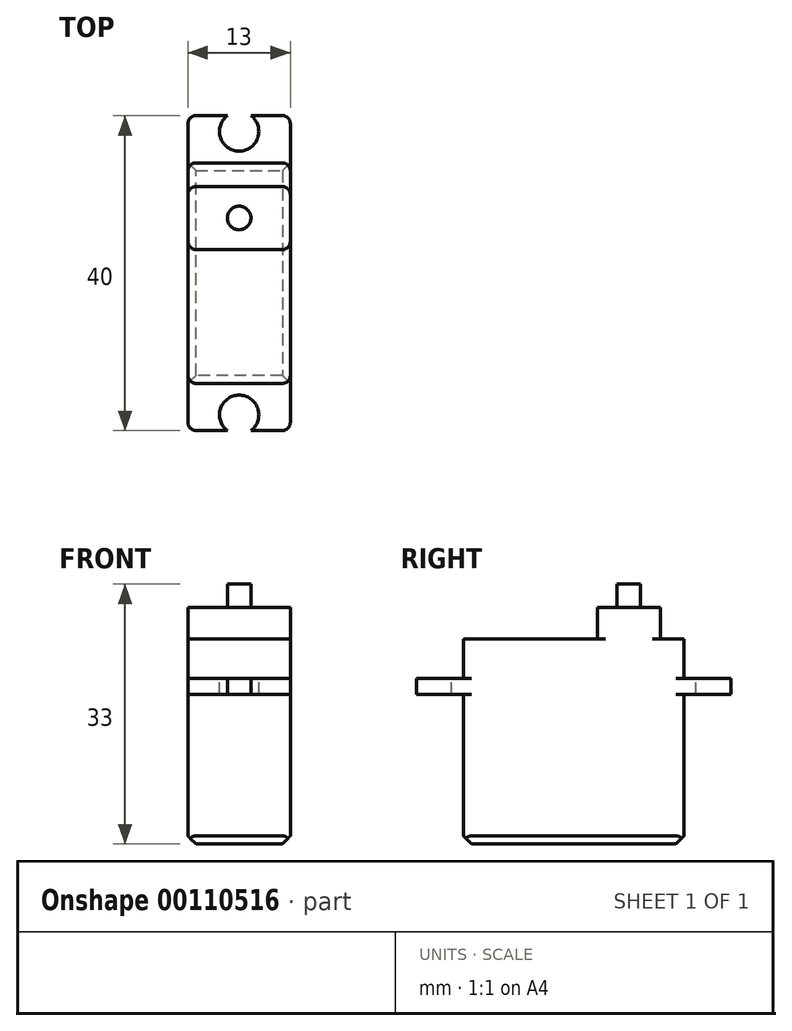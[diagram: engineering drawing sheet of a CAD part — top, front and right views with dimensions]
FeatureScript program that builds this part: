
annotation { "Feature Type Name" : "Feature", "Feature Type Description" : "" }
export const myFeature = defineFeature(function(context is Context, id is Id, definition is map)
    precondition{}
    {
        {
            var Q0;
            Q0=qCreatedBy(makeId("Right.planeOp"),FACE);
            var sketch = newSketch(context, id + "F0", { "sketchPlane" : qUnion([Q0])});
            skLineSegment(sketch, "E0", {"start": v(0, 19) * mm, "end": v(0, 0) * mm});
            skLineSegment(sketch, "E1", {"start": v(0, 0) * mm, "end": v(-28, 0) * mm});
            skLineSegment(sketch, "E2", {"start": v(-28, 0) * mm, "end": v(-28, 19) * mm});
            skLineSegment(sketch, "E3", {"start": v(-28, 19) * mm, "end": v(-34, 19) * mm});
            skLineSegment(sketch, "E4", {"start": v(-34, 19) * mm, "end": v(-34, 21) * mm});
            skLineSegment(sketch, "E5", {"start": v(6, 21) * mm, "end": v(6, 19) * mm});
            skLineSegment(sketch, "E6", {"start": v(6, 19) * mm, "end": v(0, 19) * mm});
            skLineSegment(sketch, "E7", {"start": v(-34, 21) * mm, "end": v(-28, 21) * mm});
            skLineSegment(sketch, "E8", {"start": v(-28, 21) * mm, "end": v(-28, 26) * mm});
            skLineSegment(sketch, "E9", {"start": v(-28, 26) * mm, "end": v(0, 26) * mm});
            skLineSegment(sketch, "E10", {"start": v(0, 26) * mm, "end": v(0, 21) * mm});
            skLineSegment(sketch, "E11", {"start": v(0, 21) * mm, "end": v(6, 21) * mm});
            skLineSegment(sketch, "E12", {"start": v(-11, 26) * mm, "end": v(-11, 30) * mm});
            skLineSegment(sketch, "E13", {"start": v(-11, 30) * mm, "end": v(-3, 30) * mm});
            skLineSegment(sketch, "E14", {"start": v(-3, 30) * mm, "end": v(-3, 26) * mm});
            skLineSegment(sketch, "E15", {"start": v(-7, 30) * mm, "end": v(-7, 0) * mm, "construction": true});
            skSolve(sketch);
        }
        {
            var Q0;
            Q0 = qSketchRegion(id + "F0", true);
            extrude(context, id + "F1", {"entities" : qUnion([Q0]), "endBound" : BoundingType.SYMMETRIC, "depth" : 13 * mm});
        }
        {
            var Q0;
            Q0=makeQuery(id+"F1.opExtrude","SWEPT_FACE",FACE,{"disambiguationData":[OSD([sQuery(id+"F0.wireOp",EDGE,"E13")])]});
            var sketch = newSketch(context, id + "F2", { "sketchPlane" : qUnion([Q0])});
            skCircle(sketch, "E16", {"center": v(0, -7) * mm, "radius": 1.5 * mm});
            skPoint(sketch, "E16.centerSnap0", {"position": v(6.5, -7) * mm});
            skSolve(sketch);
        }
        {
            var Q0;
            Q0 = qSketchRegion(id + "F2", true);
            extrude(context, id + "F3", {"entities" : qUnion([Q0]), "operationType" : NewBodyOperationType.ADD, "depth" : 3 * mm});
        }
        {
            var Q0;
            Q0=makeQuery(id+"F1.opExtrude","SWEPT_FACE",FACE,{"disambiguationData":[OSD([sQuery(id+"F0.wireOp",EDGE,"E1")])]});
            chamfer(context, id + "F4", {"entities" : qUnion([Q0]), "width" : 1 * mm, "tangentPropagation" : true});
        }
        {
            var Q0;
            Q0=makeQuery(id+"F1.opExtrude","CAP_EDGE",EDGE,{"disambiguationData":[OSD([sQuery(id+"F0.wireOp",EDGE,"E0")])],"isStart":false});
            var Q1;
            Q1=makeQuery(id+"F1.opExtrude","CAP_EDGE",EDGE,{"disambiguationData":[OSD([sQuery(id+"F0.wireOp",EDGE,"E10")])],"isStart":false});
            var Q2;
            Q2=makeQuery(id+"F1.opExtrude","CAP_EDGE",EDGE,{"disambiguationData":[OSD([sQuery(id+"F0.wireOp",EDGE,"E10")])],"isStart":true});
            var Q3;
            Q3=makeQuery(id+"F1.opExtrude","CAP_EDGE",EDGE,{"disambiguationData":[OSD([sQuery(id+"F0.wireOp",EDGE,"E14")])],"isStart":false});
            var Q4;
            Q4=makeQuery(id+"F1.opExtrude","CAP_EDGE",EDGE,{"disambiguationData":[OSD([sQuery(id+"F0.wireOp",EDGE,"E12")])],"isStart":false});
            var Q5;
            Q5=makeQuery(id+"F1.opExtrude","CAP_EDGE",EDGE,{"disambiguationData":[OSD([sQuery(id+"F0.wireOp",EDGE,"E12")])],"isStart":true});
            var Q6;
            Q6=makeQuery(id+"F1.opExtrude","CAP_EDGE",EDGE,{"disambiguationData":[OSD([sQuery(id+"F0.wireOp",EDGE,"E14")])],"isStart":true});
            var Q7;
            Q7=makeQuery(id+"F1.opExtrude","CAP_EDGE",EDGE,{"disambiguationData":[OSD([sQuery(id+"F0.wireOp",EDGE,"E8")])],"isStart":false});
            var Q8;
            Q8=makeQuery(id+"F1.opExtrude","CAP_EDGE",EDGE,{"disambiguationData":[OSD([sQuery(id+"F0.wireOp",EDGE,"E8")])],"isStart":true});
            var Q9;
            Q9=makeQuery(id+"F1.opExtrude","CAP_EDGE",EDGE,{"disambiguationData":[OSD([sQuery(id+"F0.wireOp",EDGE,"E4")])],"isStart":false});
            var Q10;
            Q10=makeQuery(id+"F1.opExtrude","CAP_EDGE",EDGE,{"disambiguationData":[OSD([sQuery(id+"F0.wireOp",EDGE,"E4")])],"isStart":true});
            var Q11;
            Q11=makeQuery(id+"F1.opExtrude","CAP_EDGE",EDGE,{"disambiguationData":[OSD([sQuery(id+"F0.wireOp",EDGE,"E2")])],"isStart":false});
            var Q12;
            Q12=makeQuery(id+"F1.opExtrude","CAP_EDGE",EDGE,{"disambiguationData":[OSD([sQuery(id+"F0.wireOp",EDGE,"E2")])],"isStart":true});
            var Q13;
            Q13=makeQuery(id+"F1.opExtrude","CAP_EDGE",EDGE,{"disambiguationData":[OSD([sQuery(id+"F0.wireOp",EDGE,"E5")])],"isStart":false});
            var Q14;
            Q14=makeQuery(id+"F1.opExtrude","CAP_EDGE",EDGE,{"disambiguationData":[OSD([sQuery(id+"F0.wireOp",EDGE,"E5")])],"isStart":true});
            fillet(context, id + "F5", {"entities" : qUnion([Q0, Q1, Q2, Q3, Q4, Q5, Q6, Q7, Q8, Q9, Q10, Q11, Q12, Q13, Q14]), "radius" : 1 * mm, "tangentPropagation" : true, "allowEdgeOverflow" : false});
        }
        {
            var Q0;
            Q0=makeQuery(id+"F1.opExtrude","SWEPT_FACE",FACE,{"disambiguationData":[OSD([sQuery(id+"F0.wireOp",EDGE,"E11")])]});
            var sketch = newSketch(context, id + "F6", { "sketchPlane" : qUnion([Q0])});
            skCircle(sketch, "E17", {"center": v(0, 4) * mm, "radius": 2.5 * mm});
            skCircle(sketch, "E18", {"center": v(0, -32) * mm, "radius": 2.5 * mm});
            skSolve(sketch);
        }
        {
            var Q0;
            Q0 = qSketchRegion(id + "F6", true);
            extrude(context, id + "F7", {"entities" : qUnion([Q0]), "operationType" : NewBodyOperationType.REMOVE, "oppositeDirection" : true, "depth" : 25 * mm});
        }
    });
